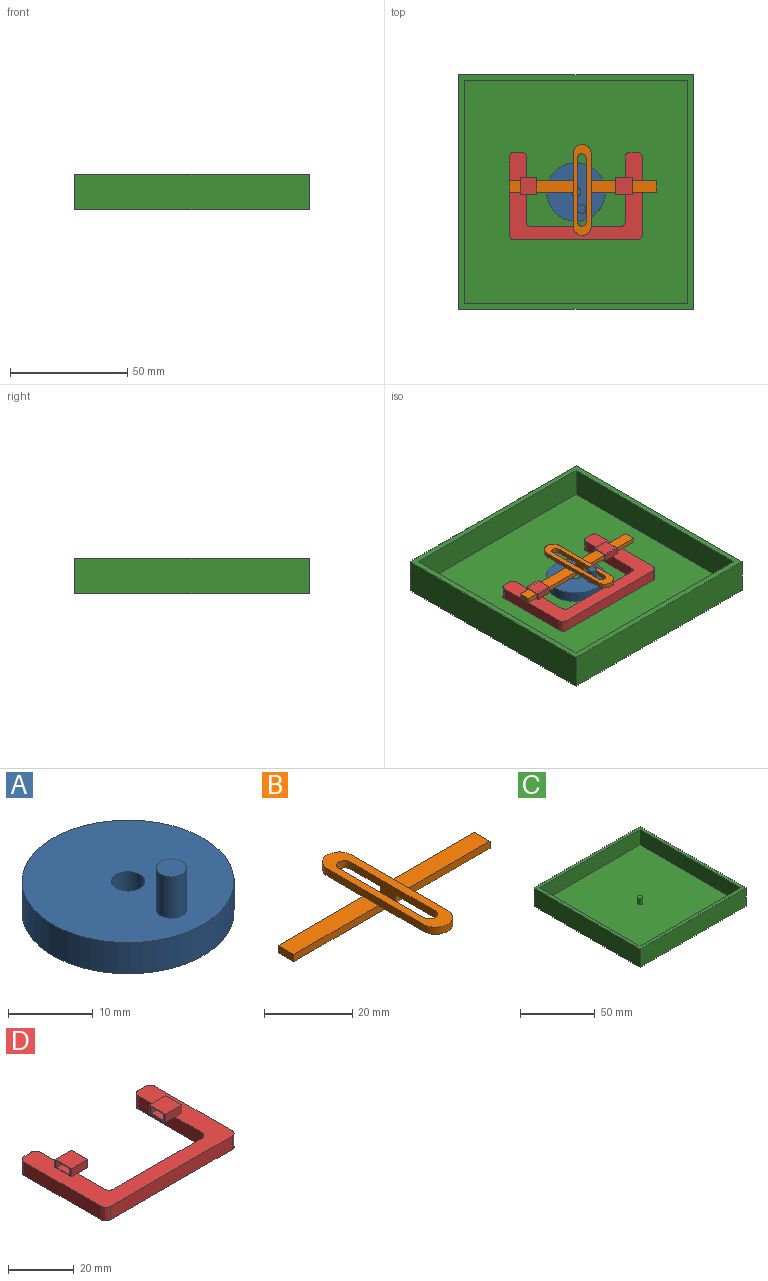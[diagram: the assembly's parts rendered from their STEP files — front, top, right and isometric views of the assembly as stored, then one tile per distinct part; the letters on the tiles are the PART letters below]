
ASSEMBLY  parts=4 mates=2
PART A: 6 faces, bbox 25x25x10.5 mm
  f0: cylinder r=1.97mm len=4.5mm, axis (0,0,-1), area 55.8mm2, adj f2,f3
  f1: cylinder r=12.5mm len=25mm, axis (0,0,-1), area 353.4mm2, adj f2,f3
  f2: plane 25x25mm, normal (0,0,1), area 468.5mm2, adj f0,f1,f4
  f3: plane 25x25mm, normal (0,0,-1), area 478.6mm2, adj f0,f1
  f4: cylinder r=1.8mm len=6mm, axis (0,0,-1), area 67.9mm2, adj f2,f5
  f5: plane 3.6x3.6mm, normal (0,0,1), area 10.2mm2, adj f4
PART B: 21 faces, bbox 63x38.6x4 mm
  f0: plane 30.15x2mm, normal (0,1,0), area 60.3mm2, adj f3,f4,f8,f16,f20
  f1: plane 30.15x2mm, normal (0,-1,0), area 60.3mm2, adj f3,f4,f8,f10,f16
  f2: plane 29.18x5mm, normal (0,0,-1), area 145.9mm2, adj f5,f6,f7,f14
  f3: plane 30.15x5mm, normal (0,0,-1), area 150.8mm2, adj f0,f1,f8,f16
  f4: plane 28x5mm, normal (0,0,1), area 140mm2, adj f0,f1,f8,f18
  f5: plane 29.18x2mm, normal (0,1,0), area 58.4mm2, adj f2,f6,f9,f14,f20
  f6: plane 5x2mm, normal (-1,0,0), area 10mm2, adj f2,f5,f7,f9
  f7: plane 29.18x2mm, normal (0,-1,0), area 58.4mm2, adj f2,f6,f9,f10,f14
  f8: plane 5x2mm, normal (1,0,0), area 10mm2, adj f0,f1,f3,f4
  f9: plane 27.26x5mm, normal (0,0,1), area 136.3mm2, adj f5,f6,f7,f12
  f10: plane 18.28x7.74mm, normal (0,0,-1), area 83.7mm2, adj f1,f7,f12,f13,f14,f16,f17,f18
  f11: cylinder r=3.87mm len=7.74mm, axis (0,0,-1), area 24.3mm2, adj f12,f18,f19,f20
  f12: plane 30.84x2mm, normal (-1,0,0), area 61.7mm2, adj f9,f10,f11,f13,f19,f20
  f13: cylinder r=3.87mm len=7.74mm, axis (0,0,-1), area 24.3mm2, adj f10,f12,f18,f19
  f14: plane 27.17x4mm, normal (1,0,0), area 64.3mm2, adj f2,f5,f7,f10,f15,f17,f19,f20
  f15: cylinder r=1.84mm len=3.67mm, axis (0,0,-1), area 11.5mm2, adj f14,f16,f19,f20
  f16: plane 27.17x4mm, normal (-1,0,0), area 64.3mm2, adj f0,f1,f3,f10,f15,f17,f19,f20
  f17: cylinder r=1.84mm len=3.67mm, axis (0,0,-1), area 11.5mm2, adj f10,f14,f16,f19
  f18: plane 30.84x2mm, normal (1,0,0), area 61.7mm2, adj f4,f10,f11,f13,f19,f20
  f19: plane 38.58x7.74mm, normal (0,0,1), area 175.6mm2, adj f11,f12,f13,f14,f15,f16,f17,f18
  f20: plane 15.3x7.74mm, normal (0,0,-1), area 71.5mm2, adj f0,f5,f11,f12,f14,f15,f16,f18
PART C: 13 faces, bbox 100x100x15 mm
  f0: plane 100x100mm, normal (0,0,1), area 975mm2, adj f1,f2,f3,f4,f6,f7,f8,f9
  f1: plane 100x15mm, normal (-1,0,0), area 1500mm2, adj f0,f2,f4,f5
  f2: plane 100x15mm, normal (0,-1,0), area 1500mm2, adj f0,f1,f3,f5
  f3: plane 100x15mm, normal (1,0,0), area 1500mm2, adj f0,f2,f4,f5
  f4: plane 100x15mm, normal (0,1,0), area 1500mm2, adj f0,f1,f3,f5
  f5: plane 100x100mm, normal (0,0,-1), area 10000mm2, adj f1,f2,f3,f4
  f6: plane 95x12.5mm, normal (1,0,0), area 1187.5mm2, adj f0,f7,f9,f10
  f7: plane 95x12.5mm, normal (0,1,0), area 1187.5mm2, adj f0,f6,f8,f10
  f8: plane 95x12.5mm, normal (-1,0,0), area 1187.5mm2, adj f0,f7,f9,f10
  f9: plane 95x12.5mm, normal (0,-1,0), area 1187.5mm2, adj f0,f6,f8,f10
  f10: plane 95x95mm, normal (0,0,1), area 9015mm2, adj f6,f7,f8,f9,f12
  f11: plane 3.56x3.56mm, normal (0,0,1), area 10mm2, adj f12
  f12: cylinder r=1.78mm len=5mm, axis (0,0,-1), area 55.9mm2, adj f10,f11
PART D: 38 faces, bbox 56.5x37.3x8 mm
  f0: plane 7x3mm, normal (1,0,0), area 8mm2, adj f4,f27,f28,f29,f34,f35,f36,f37
  f1: plane 7x3mm, normal (-1,0,0), area 8mm2, adj f26,f27,f28,f29,f34,f35,f36,f37
  f2: plane 7x3mm, normal (-1,0,0), area 8mm2, adj f4,f23,f24,f25,f30,f31,f32,f33
  f3: plane 7x3mm, normal (1,0,0), area 8mm2, adj f22,f23,f24,f25,f30,f31,f32,f33
  f4: plane 56.47x37.28mm, normal (0,0,1), area 735mm2, adj f0,f2,f5,f6,f7,f8,f9,f10
  f5: cylinder r=2mm len=5mm, axis (0,0,-1), area 15.7mm2, adj f4,f6,f20,f21
  f6: plane 38.11x5mm, normal (0,1,0), area 190.5mm2, adj f4,f5,f7,f21
  f7: cylinder r=2mm len=5mm, axis (0,0,-1), area 15.7mm2, adj f4,f6,f8,f21
  f8: plane 27.53x5mm, normal (1,0,0), area 137.6mm2, adj f4,f7,f9,f21,f22
  f9: cylinder r=2mm len=5mm, axis (0,0,-1), area 15.7mm2, adj f4,f8,f10,f21
  f10: plane 5x3.18mm, normal (0,1,0), area 15.9mm2, adj f4,f9,f11,f21
  f11: cylinder r=2mm len=5mm, axis (0,0,-1), area 15.7mm2, adj f4,f10,f12,f21
  f12: plane 33.28x5mm, normal (-1,0,0), area 166.4mm2, adj f4,f11,f13,f21
  f13: cylinder r=2mm len=5mm, axis (0,0,-1), area 15.7mm2, adj f4,f12,f14,f21
  f14: plane 52.47x5mm, normal (0,-1,0), area 262.4mm2, adj f4,f13,f15,f21
  f15: cylinder r=2mm len=5mm, axis (0,0,-1), area 15.7mm2, adj f4,f14,f16,f21
  f16: plane 33.28x5mm, normal (1,0,0), area 166.4mm2, adj f4,f15,f17,f21
  f17: cylinder r=2mm len=5mm, axis (0,0,-1), area 15.7mm2, adj f4,f16,f18,f21
  f18: plane 5x3.18mm, normal (0,1,0), area 15.9mm2, adj f4,f17,f19,f21
  f19: cylinder r=2mm len=5mm, axis (0,0,-1), area 15.7mm2, adj f4,f18,f20,f21
  f20: plane 27.53x5mm, normal (-1,0,0), area 137.6mm2, adj f4,f5,f19,f21,f26
  f21: plane 56.47x37.28mm, normal (0,0,-1), area 774.3mm2, adj f5,f6,f7,f8,f9,f10,f11,f12
  f22: plane 7x4.4mm, normal (0,0,-1), area 30.8mm2, adj f3,f8,f23,f24
  f23: plane 7x3mm, normal (0,1,0), area 21mm2, adj f2,f3,f4,f22,f25
  f24: plane 7x3mm, normal (0,-1,0), area 21mm2, adj f2,f3,f4,f22,f25
  f25: plane 7x7mm, normal (0,0,1), area 49mm2, adj f2,f3,f23,f24
  f26: plane 7x3.99mm, normal (0,0,-1), area 28mm2, adj f1,f20,f27,f28
  f27: plane 7x3mm, normal (0,-1,0), area 21mm2, adj f0,f1,f4,f26,f29
  f28: plane 7x3mm, normal (0,1,0), area 21mm2, adj f0,f1,f4,f26,f29
  f29: plane 7x7mm, normal (0,0,1), area 49mm2, adj f0,f1,f27,f28
  f30: plane 7x2.36mm, normal (0,1,0), area 16.5mm2, adj f2,f3,f31,f33
  f31: plane 7x5.5mm, normal (0,0,-1), area 38.5mm2, adj f2,f3,f30,f32
  f32: plane 7x2.36mm, normal (0,-1,0), area 16.5mm2, adj f2,f3,f31,f33
  f33: plane 7x5.5mm, normal (0,0,1), area 38.5mm2, adj f2,f3,f30,f32
  f34: plane 7x2.36mm, normal (0,-1,0), area 16.5mm2, adj f0,f1,f35,f37
  f35: plane 7x5.5mm, normal (0,0,-1), area 38.5mm2, adj f0,f1,f34,f36
  f36: plane 7x2.36mm, normal (0,1,0), area 16.5mm2, adj f0,f1,f35,f37
  f37: plane 7x5.5mm, normal (0,0,1), area 38.5mm2, adj f0,f1,f34,f36
PLACE A rot(axis=(0,0,1),21.8deg) t=(24.36,-28.22,-17.42)mm
PLACE B t=(5.1,-13.48,-17.42)mm
PLACE C t=(2.23,-13.23,-17.42)mm fixed
PLACE D t=(2.23,-13.23,-17.42)mm fixed
MATE pin_slot C.f12 <-> A.f0  axis (0,0,1) through (52.23,36.77,-9.92)mm
MATE planar B.f7 <-> D.f30  axis (0,-1,0) through (38.28,36.61,-8.42)mm
